# Revit family: 2093089 Sylvania Lighting Fixture MC2 D I 1-2M 3K DALI WHT OPAL
name_source: partatom
category: Lighting Fixtures
revit_build: Autodesk Revit 2016 (Build: 20150220_1215(x64)
units: mm (PartAtom-declared; Revit-internal decimal feet)

## family parameters
Cut with Voids When Loaded = No
Host = Face
Light Source = Yes
OmniClass Number = 23.80.70.11.17
OmniClass Title = Specialized Lighting by Location or Use
Part Type = Normal
Room Calculation Point = No
Round Connector Dimension = Use Diameter
Shared = No

## types (1)
- 2093089 MC2 D/I 1.2M 3K DALI WHT OPAL
    Apparent Load = 32 VA
    Assembly Code = D5020200
    AssetType = Fixed
    Color Filter = 16777215
    Default Elevation = 0 mm  [stored 0 ft]
    Description = 2093089   MC2 D/I 1.2M 3K DALI WHT OPAL  Continuous lines of LED light, white RAL 9016, direct/indirect distribution (65/35), various accessories available, compact and minimalist design based on the Golden Mean, ideal for offices, meeting rooms, corridors, education facilities, museums and libraries, extruded aluminium body, diffuser: opal, colour temperature: 3000K warm white, total system power: 32W, total fixture output: 3833lm, luminaire efficacy: 120lm/W, LOR: 100%, colour rendering: Ra >80, LED Chromacity: 1 step MacAdam ellipse, lifetime: 60,000 hours at 90% of the original output (L90), energy class: A++, A+, A, IR/UV free light source without heat radiation, operating voltage: 220-240V / 50-60Hz, drive current: (Direct) 800mA + (Indirect) 350mA, electronic driver, DALI dimmable, direct/indirect independently addressable, electrical protection: CLASS I, IP20, suitable for internal environment only.
    Dimming Lamp Color Temperature Shift = <None>
    DocumentationLiterature = http://www.sylvania-lighting.com
    DurationUnit = hours
    ElectricShockClassification = Class I
    Emit Shape Visible in Rendering = No
    Emit from Rectangle Length = 1200 mm  [stored 3.93701 ft]
    Emit from Rectangle Width = 52 mm  [stored 0.170604 ft]
    ExpectedLife = 50000
    Height_SYL = 86 mm  [stored 0.282152 ft]
    IfcExportAs = IfcLightFixtureType
    IfcExportType = IfcLightFixtureType
    IngressProtection = IP20
    Keynote = 16500
    Lamp = LED
    LampColourRenderingIndex = 80
    LampColourTemperature = 3000 K
    LampMacAdamStep = 3
    LampNominalLuminous = 3833 lm
    LampsType = LED
    Length_SYL = 1200 mm  [stored 3.93701 ft]
    LightOutputRatio = 100
    LuminousEfficacy = 120 lm/W
    Manufacturer = Feilo Sylvania
    ManufacturerName = Feilo Sylvania
    Material = aluminium housing, polycarbonate diffuser
    Material_1_SYL = Metal_Sylvania_Mini Continuum II_White
    Material_2_SYL = Polycarbonate_Sylvania_Mini Continuum II_Opal_4000K
    Material_3_SYL = Metal_Sylvania_Mini Contiuum II_Silver
    Material_4_SYL = Metal_Sylvania_Mini Contiuum II_Silver
    Model = MC2 D/I 1.2M 3K DALI WHT OPAL
    ModelNumber = 2093089
    ModelReference = MC2 D/I 1.2M 3K DALI WHT OPAL
    Name = MC2 D/I 1.2M 3K DALI WHT OPAL
    NominalHeight = 86 mm  [stored 0.282152 ft]
    NominalLength = 1200 mm  [stored 3.93701 ft]
    NominalWidth = 0 mm  [stored 0 ft]
    Photometric Web File = 2093089.ies
    PowerConsumption = 32 W
    PowerFactor = 0.95
    Tilt Angle = -90.00°
    TypeName = MC2 D/I 1.2M 3K DALI WHT OPAL
    URL = http://www.sylvania-lighting.com
    Voltage = 0 V
    Weight = 3.1 kg
    Width_SYL = 54 mm  [stored 0.177165 ft]

note: [stored X ft] marks values corroborated as IEEE doubles in the binary element streams (Revit-internal decimal feet)

## geometry (parser evidence)
native form markers: Sweep x3
no freeform markers — native parametric forms only
